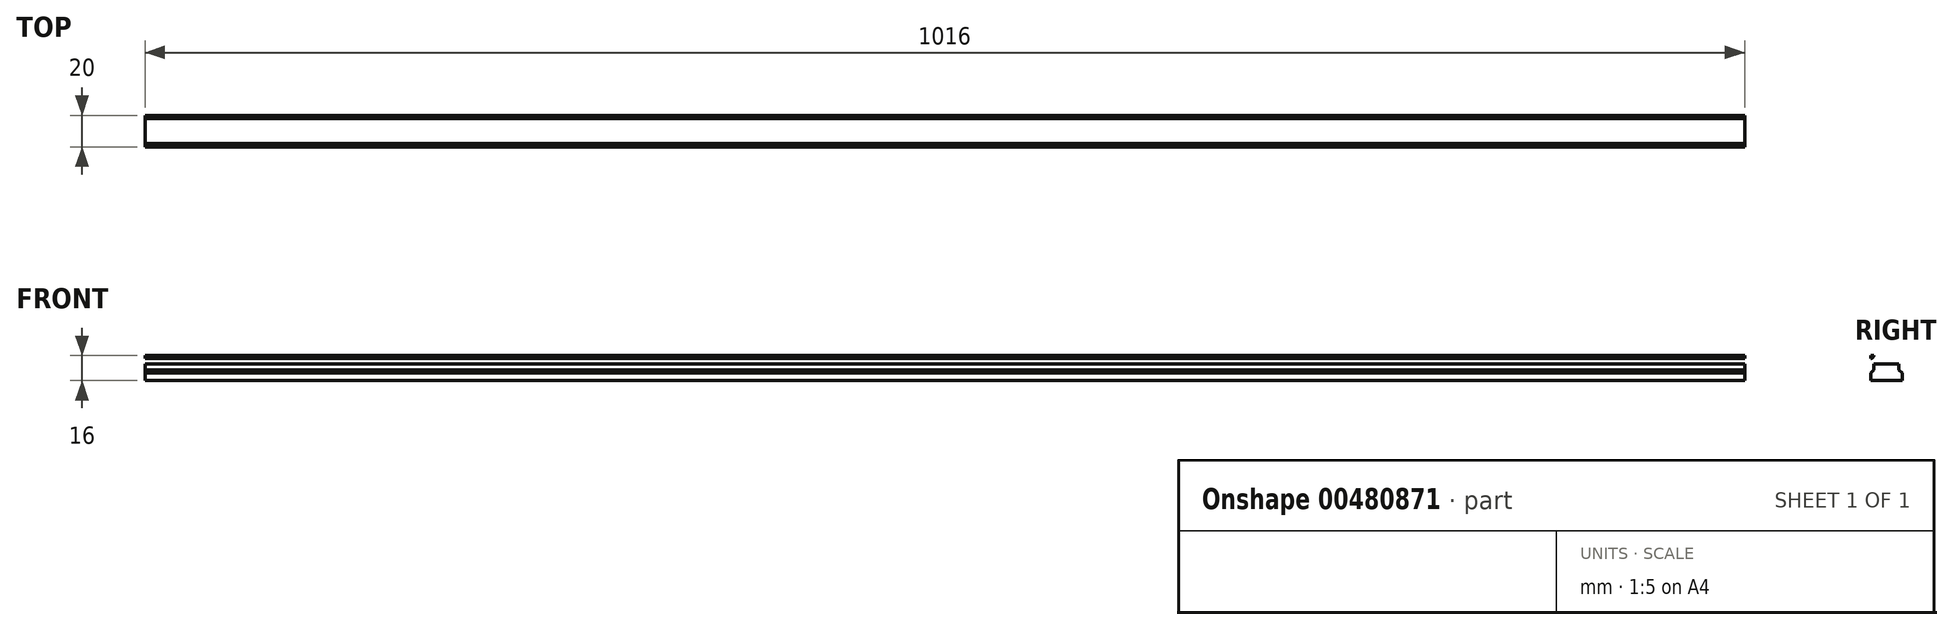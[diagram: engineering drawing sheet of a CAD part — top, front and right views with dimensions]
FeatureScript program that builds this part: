
annotation { "Feature Type Name" : "Feature", "Feature Type Description" : "" }
export const myFeature = defineFeature(function(context is Context, id is Id, definition is map)
    precondition{}
    {
        {
            var Q0;
            Q0=qCreatedBy(makeId("Right.planeOp"),FACE);
            var sketch = newSketch(context, id + "F0", { "sketchPlane" : qUnion([Q0])});
            skLineSegment(sketch, "E0.bottom", {"start": v(-7.15, 22.88) * mm, "end": v(-27.15, 22.88) * mm});
            skLineSegment(sketch, "E0.top", {"start": v(-7.15, 38.88) * mm, "end": v(-27.15, 38.88) * mm});
            skLineSegment(sketch, "E0.left", {"start": v(-7.15, 22.88) * mm, "end": v(-7.15, 38.88) * mm});
            skLineSegment(sketch, "E0.right", {"start": v(-27.15, 22.88) * mm, "end": v(-27.15, 38.88) * mm});
            skPoint(sketch, "E0.middle", {"position": v(-17.15, 30.88) * mm});
            skArc(sketch, "E1", {"start": v(-25.15, 38.88) * mm, "mid": v(-25.74, 37.46) * mm, "end": v(-27.15, 36.88) * mm});
            skArc(sketch, "E2", {"start": v(-9.15, 38.88) * mm, "mid": v(-8.57, 37.46) * mm, "end": v(-7.15, 36.88) * mm});
            skLineSegment(sketch, "E3", {"start": v(-27.15, 27.58) * mm, "end": v(-25.15, 29.58) * mm});
            skLineSegment(sketch, "E4", {"start": v(-25.15, 29.58) * mm, "end": v(-25.15, 33.39) * mm});
            skLineSegment(sketch, "E5", {"start": v(-7.15, 27.58) * mm, "end": v(-9.15, 29.58) * mm});
            skLineSegment(sketch, "E6", {"start": v(-9.15, 29.58) * mm, "end": v(-9.15, 33.39) * mm});
            skLineSegment(sketch, "E7", {"start": v(-27.15, 33.39) * mm, "end": v(-7.15, 33.39) * mm});
            skArc(sketch, "E8", {"start": v(-27.15, 35.39) * mm, "mid": v(-25.74, 34.8) * mm, "end": v(-25.15, 33.39) * mm});
            skArc(sketch, "E9", {"start": v(-7.15, 35.39) * mm, "mid": v(-8.57, 34.8) * mm, "end": v(-9.15, 33.39) * mm});
            skSolve(sketch);
        }
        {
            var Q0;
            {var subQ2=sQuery(id+"F0.wireOp",EDGE,"E0.bottom");Q0=makeQuery(id+"F0.imprint","IMPRINT",FACE,{"disambiguationData":[TD([[makeQuery(id+"F0.imprint","IMPRINT",EDGE,{"derivedFrom":subQ2}),-1.0]])]});}
            var Q1;
            {var subQ0=sQuery(id+"F0.wireOp",EDGE,"E1");Q1=makeQuery(id+"F0.imprint","IMPRINT",FACE,{"disambiguationData":[TD([[makeQuery(id+"F0.imprint","IMPRINT",EDGE,{"derivedFrom":subQ0}),1.0]])]});}
            extrude(context, id + "F1", {"entities" : qUnion([Q0, Q1]), "depth" : 1016 * mm});
        }
    });
